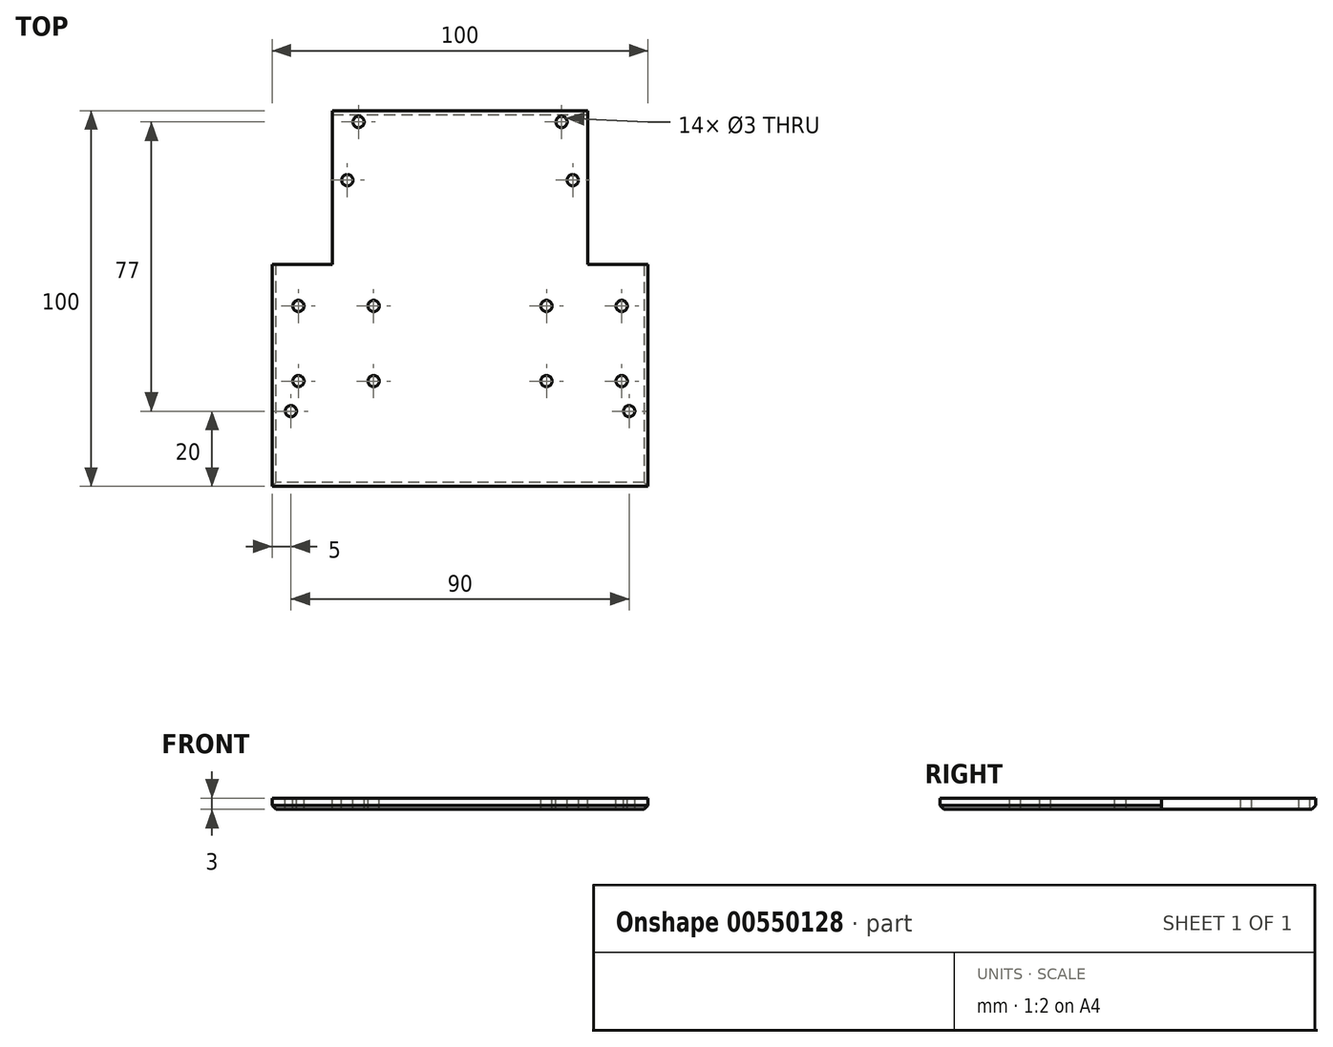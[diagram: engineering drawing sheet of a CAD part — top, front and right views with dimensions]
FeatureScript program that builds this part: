
annotation { "Feature Type Name" : "Feature", "Feature Type Description" : "" }
export const myFeature = defineFeature(function(context is Context, id is Id, definition is map)
    precondition{}
    {
        {
            var Q0;
            Q0=qCreatedBy(makeId("Top.planeOp"),FACE);
            var sketch = newSketch(context, id + "F0", { "sketchPlane" : qUnion([Q0])});
            skLineSegment(sketch, "E0.bottom", {"start": v(50, -50) * mm, "end": v(-50, -50) * mm});
            skLineSegment(sketch, "E0.top", {"start": v(50, 50) * mm, "end": v(-50, 50) * mm});
            skLineSegment(sketch, "E0.left", {"start": v(50, -50) * mm, "end": v(50, 50) * mm});
            skLineSegment(sketch, "E0.right", {"start": v(-50, -50) * mm, "end": v(-50, 50) * mm});
            skPoint(sketch, "E0.middle", {"position": v(0, 0) * mm});
            skSolve(sketch);
        }
        {
            var Q0;
            Q0=makeQuery(id+"F0.imprint","IMPRINT",FACE,{"disambiguationData":[TD([[makeQuery(id+"F0.imprint","IMPRINT",EDGE,{"derivedFrom":sQuery(id+"F0.wireOp",EDGE,"E0.bottom")}),-1.0]])]});
            extrude(context, id + "F1", {"entities" : qUnion([Q0]), "depth" : 3 * mm, "offsetDistance" : 25 * mm});
        }
        {
            var Q0;
            Q0=makeQuery(id+"F1.opExtrude","CAP_FACE",FACE,{"disambiguationData":[OSD([sQuery(id+"F0.wireOp",EDGE,"E0.bottom"),sQuery(id+"F0.wireOp",EDGE,"E0.top"),sQuery(id+"F0.wireOp",EDGE,"E0.left"),sQuery(id+"F0.wireOp",EDGE,"E0.right")])],"isStart":false});
            var sketch = newSketch(context, id + "F2", { "sketchPlane" : qUnion([Q0])});
            skPoint(sketch, "E1", {"position": v(30, 31.5) * mm});
            skPoint(sketch, "E2.MirrorP", {"position": v(-30, 31.5) * mm});
            skSolve(sketch);
        }
        {
            var Q0;
            Q0=sQuery(id+"F2.wireOp",VERTEX,"E2.MirrorP");
            var Q1;
            Q1=sQuery(id+"F2.wireOp",VERTEX,"E1");
            var Q2;
            Q2=makeQuery(id+"F1.opExtrude","SWEPT_BODY",BODY,{"disambiguationData":[OSD([sQuery(id+"F0.wireOp",EDGE,"E0.bottom"),sQuery(id+"F0.wireOp",EDGE,"E0.top"),sQuery(id+"F0.wireOp",EDGE,"E0.left"),sQuery(id+"F0.wireOp",EDGE,"E0.right")])]});
            hole(context, id + "F3", {"style" : HoleStyle.SIMPLE, "endStyle" : HoleEndStyle.THROUGH, "holeDiameter" : 3 * mm, "isTappedThrough" : true, "tappedDepth" : 12 * mm, "tapClearance" : 3, "locations" : qUnion([Q0, Q1]), "scope" : qUnion([Q2])});
        }
        {
            var Q0;
            Q0=makeQuery(id+"F1.opExtrude","CAP_FACE",FACE,{"disambiguationData":[OSD([sQuery(id+"F0.wireOp",EDGE,"E0.bottom"),sQuery(id+"F0.wireOp",EDGE,"E0.top"),sQuery(id+"F0.wireOp",EDGE,"E0.left"),sQuery(id+"F0.wireOp",EDGE,"E0.right")])],"isStart":false});
            var sketch = newSketch(context, id + "F4", { "sketchPlane" : qUnion([Q0])});
            skLineSegment(sketch, "E3", {"start": v(-34, 50) * mm, "end": v(-34, 9) * mm});
            skLineSegment(sketch, "E4", {"start": v(-34, 9) * mm, "end": v(-50, 9) * mm});
            skLineSegment(sketch, "E5.MirrorCS", {"start": v(34, 50) * mm, "end": v(34, 9) * mm});
            skLineSegment(sketch, "E6.MirrorCS", {"start": v(34, 9) * mm, "end": v(50, 9) * mm});
            skSolve(sketch);
        }
        {
            var Q0;
            {var subQ0=sQuery(id+"F4.wireOp",EDGE,"E3");Q0=makeQuery(id+"F4.imprint","IMPRINT",FACE,{"disambiguationData":[TD([[makeQuery(id+"F4.imprint","IMPRINT",EDGE,{"derivedFrom":subQ0}),-1.0]])]});}
            var Q1;
            {var subQ0=sQuery(id+"F4.wireOp",EDGE,"E5.MirrorCS");Q1=makeQuery(id+"F4.imprint","IMPRINT",FACE,{"disambiguationData":[TD([[makeQuery(id+"F4.imprint","IMPRINT",EDGE,{"derivedFrom":subQ0}),1.0]])]});}
            extrude(context, id + "F5", {"entities" : qUnion([Q0, Q1]), "operationType" : NewBodyOperationType.REMOVE, "oppositeDirection" : true, "depth" : 3 * mm, "offsetDistance" : 25 * mm});
        }
        {
            var Q0;
            Q0=makeQuery(id+"F1.opExtrude","CAP_FACE",FACE,{"disambiguationData":[OSD([sQuery(id+"F0.wireOp",EDGE,"E0.bottom"),sQuery(id+"F0.wireOp",EDGE,"E0.top"),sQuery(id+"F0.wireOp",EDGE,"E0.left"),sQuery(id+"F0.wireOp",EDGE,"E0.right")])],"isStart":false});
            var sketch = newSketch(context, id + "F6", { "sketchPlane" : qUnion([Q0])});
            skPoint(sketch, "E7", {"position": v(23, -2) * mm});
            skPoint(sketch, "E8", {"position": v(43, -2) * mm});
            skPoint(sketch, "E9", {"position": v(23, -22) * mm});
            skPoint(sketch, "E10", {"position": v(43, -22) * mm});
            skPoint(sketch, "E11.MirrorP", {"position": v(-43, -22) * mm});
            skPoint(sketch, "E12.MirrorP", {"position": v(-23, -22) * mm});
            skPoint(sketch, "E13.MirrorP", {"position": v(-23, -2) * mm});
            skPoint(sketch, "E14.MirrorP", {"position": v(-43, -2) * mm});
            skSolve(sketch);
        }
        {
            var Q0;
            Q0=sQuery(id+"F6.wireOp",VERTEX,"E14.MirrorP");
            var Q1;
            Q1=sQuery(id+"F6.wireOp",VERTEX,"E13.MirrorP");
            var Q2;
            Q2=sQuery(id+"F6.wireOp",VERTEX,"E12.MirrorP");
            var Q3;
            Q3=sQuery(id+"F6.wireOp",VERTEX,"E11.MirrorP");
            var Q4;
            Q4=sQuery(id+"F6.wireOp",VERTEX,"E7");
            var Q5;
            Q5=sQuery(id+"F6.wireOp",VERTEX,"E8");
            var Q6;
            Q6=sQuery(id+"F6.wireOp",VERTEX,"E10");
            var Q7;
            Q7=sQuery(id+"F6.wireOp",VERTEX,"E9");
            var Q8;
            Q8=makeQuery(id+"F1.opExtrude","SWEPT_BODY",BODY,{"disambiguationData":[OSD([sQuery(id+"F0.wireOp",EDGE,"E0.bottom"),sQuery(id+"F0.wireOp",EDGE,"E0.top"),sQuery(id+"F0.wireOp",EDGE,"E0.left"),sQuery(id+"F0.wireOp",EDGE,"E0.right")])]});
            hole(context, id + "F7", {"style" : HoleStyle.SIMPLE, "endStyle" : HoleEndStyle.THROUGH, "holeDiameter" : 3 * mm, "isTappedThrough" : true, "tappedDepth" : 12 * mm, "tapClearance" : 3, "locations" : qUnion([Q0, Q1, Q2, Q3, Q4, Q5, Q6, Q7]), "scope" : qUnion([Q8])});
        }
        {
            var Q0;
            Q0=makeQuery(id+"F1.opExtrude","CAP_EDGE",EDGE,{"disambiguationData":[OSD([sQuery(id+"F0.wireOp",EDGE,"E0.bottom")])],"isStart":true});
            var Q1;
            Q1=makeQuery(id+"F1.opExtrude","CAP_EDGE",EDGE,{"disambiguationData":[OSD([sQuery(id+"F0.wireOp",EDGE,"E0.right")])],"isStart":true});
            var Q2;
            Q2=makeQuery(id+"F5.boolean.opBoolean","COPY",EDGE,{"derivedFrom":makeQuery(id+"F5.opExtrude","CAP_EDGE",EDGE,{"disambiguationData":[OSD([sQuery(id+"F4.wireOp",EDGE,"E4")])],"isStart":false})});
            var Q3;
            Q3=makeQuery(id+"F5.boolean.opBoolean","COPY",EDGE,{"derivedFrom":makeQuery(id+"F5.opExtrude","CAP_EDGE",EDGE,{"disambiguationData":[OSD([sQuery(id+"F4.wireOp",EDGE,"E3")])],"isStart":false})});
            var Q4;
            Q4=makeQuery(id+"F1.opExtrude","CAP_EDGE",EDGE,{"disambiguationData":[OSD([sQuery(id+"F0.wireOp",EDGE,"E0.top")])],"isStart":true});
            var Q5;
            Q5=makeQuery(id+"F5.boolean.opBoolean","COPY",EDGE,{"derivedFrom":makeQuery(id+"F5.opExtrude","CAP_EDGE",EDGE,{"disambiguationData":[OSD([sQuery(id+"F4.wireOp",EDGE,"E5.MirrorCS")])],"isStart":false})});
            var Q6;
            Q6=makeQuery(id+"F5.boolean.opBoolean","COPY",EDGE,{"derivedFrom":makeQuery(id+"F5.opExtrude","CAP_EDGE",EDGE,{"disambiguationData":[OSD([sQuery(id+"F4.wireOp",EDGE,"E6.MirrorCS")])],"isStart":false})});
            var Q7;
            Q7=makeQuery(id+"F1.opExtrude","CAP_EDGE",EDGE,{"disambiguationData":[OSD([sQuery(id+"F0.wireOp",EDGE,"E0.left")])],"isStart":true});
            chamfer(context, id + "F8", {"entities" : qUnion([Q0, Q1, Q2, Q3, Q4, Q5, Q6, Q7]), "width" : 1 * mm, "tangentPropagation" : true});
        }
        {
            var Q0;
            Q0=makeQuery(id+"F1.opExtrude","CAP_FACE",FACE,{"disambiguationData":[OSD([sQuery(id+"F0.wireOp",EDGE,"E0.bottom"),sQuery(id+"F0.wireOp",EDGE,"E0.top"),sQuery(id+"F0.wireOp",EDGE,"E0.left"),sQuery(id+"F0.wireOp",EDGE,"E0.right")])],"isStart":false});
            var sketch = newSketch(context, id + "F9", { "sketchPlane" : qUnion([Q0])});
            skLineSegment(sketch, "E15", {"start": v(-50, -30) * mm, "end": v(50, -30) * mm});
            skLineSegment(sketch, "E16", {"start": v(-45, 9) * mm, "end": v(-45, -50) * mm});
            skLineSegment(sketch, "E17", {"start": v(45, 9) * mm, "end": v(45, -50) * mm});
            skPoint(sketch, "E18", {"position": v(-45, -30) * mm});
            skPoint(sketch, "E19", {"position": v(45, -30) * mm});
            skLineSegment(sketch, "E20", {"start": v(-27, 50) * mm, "end": v(-27, -50) * mm});
            skLineSegment(sketch, "E21", {"start": v(-34, 47) * mm, "end": v(34, 47) * mm});
            skLineSegment(sketch, "E22", {"start": v(27, -50) * mm, "end": v(27, 50) * mm});
            skPoint(sketch, "E23", {"position": v(-27, 47) * mm});
            skPoint(sketch, "E24", {"position": v(27, 47) * mm});
            skSolve(sketch);
        }
        {
            var Q0;
            Q0=sQuery(id+"F9.wireOp",VERTEX,"E18");
            var Q1;
            Q1=sQuery(id+"F9.wireOp",VERTEX,"E19");
            var Q2;
            Q2=sQuery(id+"F9.wireOp",VERTEX,"E23");
            var Q3;
            Q3=sQuery(id+"F9.wireOp",VERTEX,"E24");
            var Q4;
            Q4=makeQuery(id+"F1.opExtrude","SWEPT_BODY",BODY,{"disambiguationData":[OSD([sQuery(id+"F0.wireOp",EDGE,"E0.bottom"),sQuery(id+"F0.wireOp",EDGE,"E0.top"),sQuery(id+"F0.wireOp",EDGE,"E0.left"),sQuery(id+"F0.wireOp",EDGE,"E0.right")])]});
            hole(context, id + "F10", {"style" : HoleStyle.SIMPLE, "endStyle" : HoleEndStyle.THROUGH, "holeDiameter" : 3 * mm, "isTappedThrough" : true, "tappedDepth" : 12 * mm, "tapClearance" : 3, "locations" : qUnion([Q0, Q1, Q2, Q3]), "scope" : qUnion([Q4])});
        }
    });
